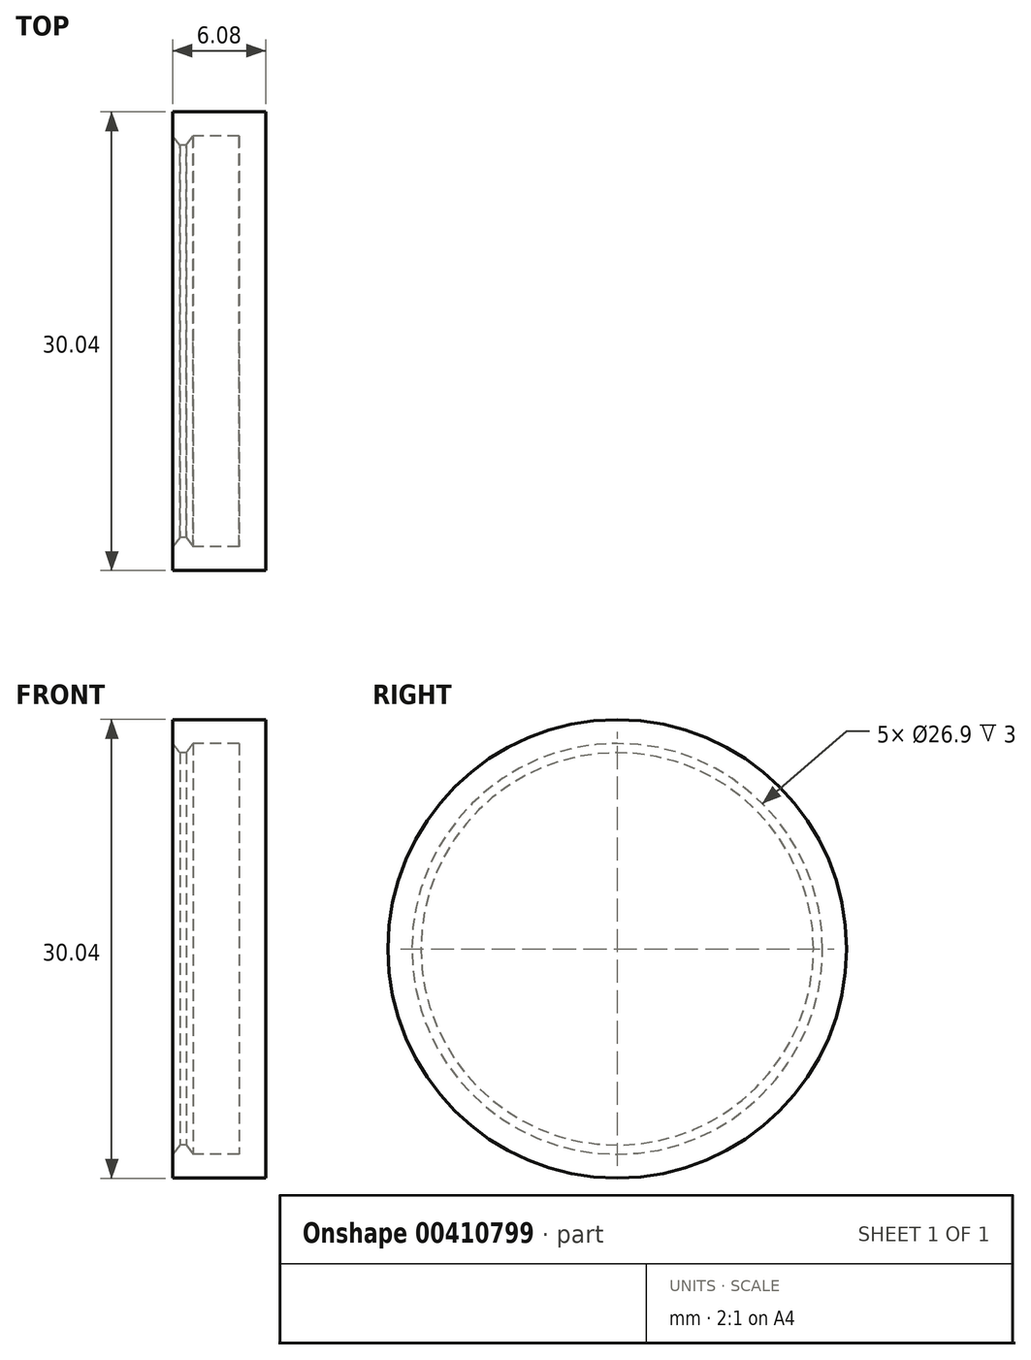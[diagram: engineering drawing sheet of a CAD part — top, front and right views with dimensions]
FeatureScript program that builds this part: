
annotation { "Feature Type Name" : "Feature", "Feature Type Description" : "" }
export const myFeature = defineFeature(function(context is Context, id is Id, definition is map)
    precondition{}
    {
        {
            var Q0;
            Q0=qCreatedBy(makeId("Front.planeOp"),FACE);
            var sketch = newSketch(context, id + "F0", { "sketchPlane" : qUnion([Q0])});
            skLineSegment(sketch, "E0", {"start": v(-32.9, 0) * mm, "end": v(30.08, 0) * mm, "construction": true});
            skLineSegment(sketch, "E1", {"start": v(-7.91, 15.02) * mm, "end": v(-7.91, 0) * mm});
            skLineSegment(sketch, "E2", {"start": v(-7.91, 0) * mm, "end": v(-9.66, 0) * mm});
            skLineSegment(sketch, "E3", {"start": v(-9.66, 0) * mm, "end": v(-9.66, 13.45) * mm});
            skLineSegment(sketch, "E4", {"start": v(-9.66, 13.45) * mm, "end": v(-12.66, 13.45) * mm});
            skLineSegment(sketch, "E5", {"start": v(-13.99, 13.45) * mm, "end": v(-13.99, 15.02) * mm});
            skLineSegment(sketch, "E6", {"start": v(-13.99, 15.02) * mm, "end": v(-7.91, 15.02) * mm});
            skPoint(sketch, "E7", {"position": v(-13.54, 12.85) * mm});
            skPoint(sketch, "E8", {"position": v(-13.11, 12.85) * mm});
            skLineSegment(sketch, "E9", {"start": v(-13.54, 12.85) * mm, "end": v(-13.11, 12.85) * mm});
            skLineSegment(sketch, "E10", {"start": v(-13.99, 13.45) * mm, "end": v(-13.54, 12.85) * mm});
            skLineSegment(sketch, "E11", {"start": v(-13.11, 12.85) * mm, "end": v(-12.66, 13.45) * mm});
            skSolve(sketch);
        }
        {
            var Q0;
            Q0=makeQuery(id+"F0.imprint","IMPRINT",FACE,{"disambiguationData":[TD([[makeQuery(id+"F0.imprint","IMPRINT",EDGE,{"derivedFrom":sQuery(id+"F0.wireOp",EDGE,"E1")}),-1.0]])]});
            var Q1;
            Q1=sQuery(id+"F0.wireOp",EDGE,"E0");
            revolve(context, id + "F1", {"entities" : qUnion([Q0]), "axis" : qUnion([Q1]), "revolveType" : RevolveType.FULL});
        }
    });
